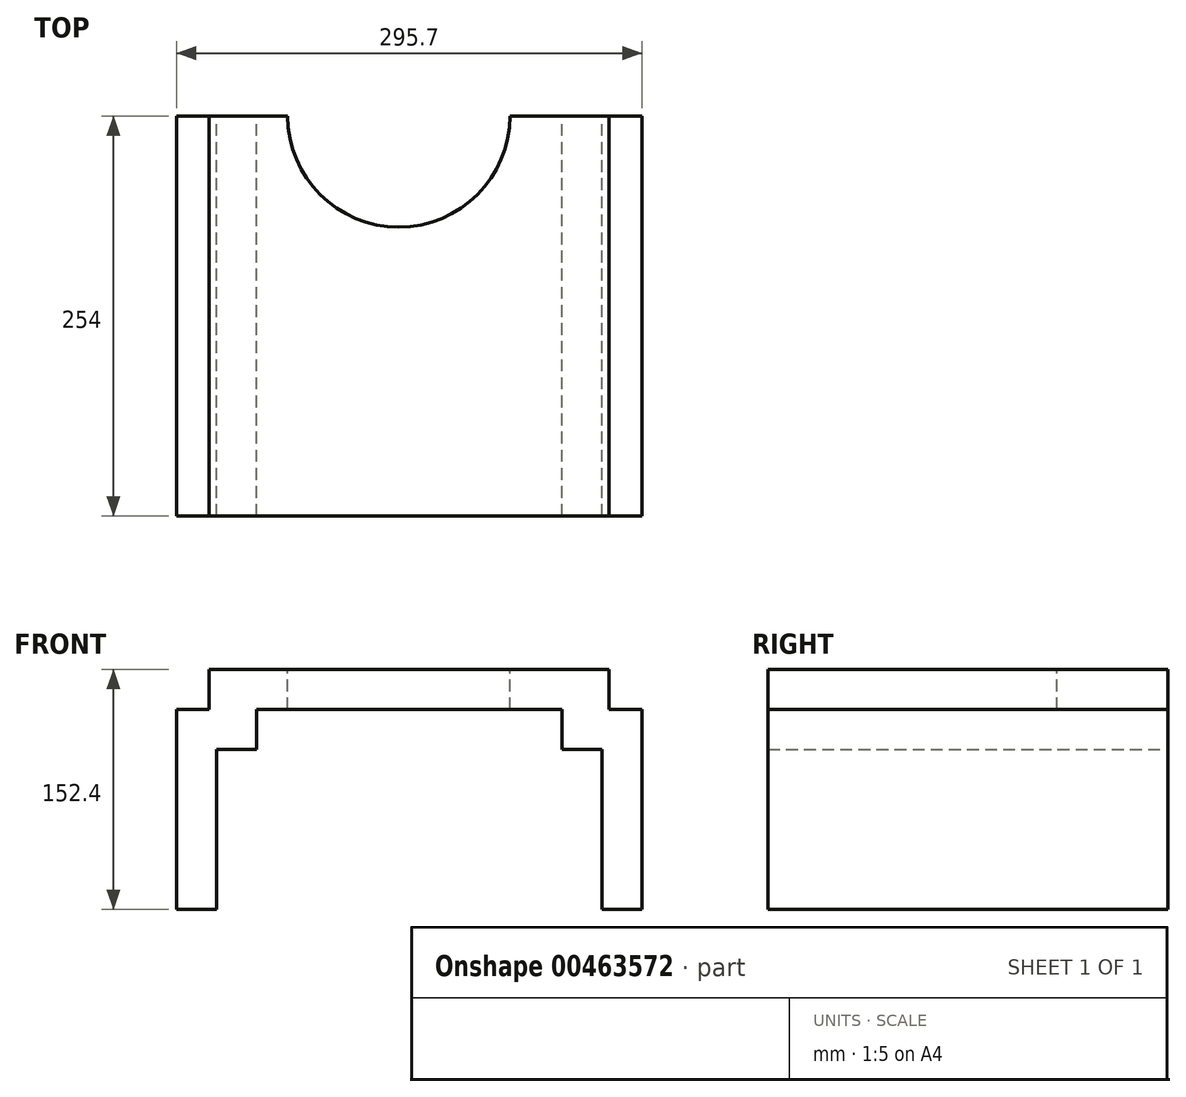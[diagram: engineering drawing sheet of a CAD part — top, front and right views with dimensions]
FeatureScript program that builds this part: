
annotation { "Feature Type Name" : "Feature", "Feature Type Description" : "" }
export const myFeature = defineFeature(function(context is Context, id is Id, definition is map)
    precondition{}
    {
        {
            var Q0;
            Q0=qCreatedBy(makeId("Front.planeOp"),FACE);
            var sketch = newSketch(context, id + "F0", { "sketchPlane" : qUnion([Q0])});
            skLineSegment(sketch, "E0.bottom", {"start": v(0, 0) * mm, "end": v(254, 0) * mm});
            skLineSegment(sketch, "E0.top", {"start": v(29.95, -25.4) * mm, "end": v(224.05, -25.4) * mm});
            skLineSegment(sketch, "E0.left", {"start": v(0, 0) * mm, "end": v(0, -25.4) * mm});
            skLineSegment(sketch, "E0.right", {"start": v(254, 0) * mm, "end": v(254, -25.4) * mm});
            skLineSegment(sketch, "E1.bottom", {"start": v(0, -25.4) * mm, "end": v(-20.85, -25.4) * mm});
            skLineSegment(sketch, "E1.top", {"start": v(4.55, -152.4) * mm, "end": v(-20.85, -152.4) * mm});
            skLineSegment(sketch, "E1.left", {"start": v(29.95, -25.4) * mm, "end": v(29.95, -50.8) * mm});
            skLineSegment(sketch, "E1.right", {"start": v(-20.85, -25.4) * mm, "end": v(-20.85, -152.4) * mm});
            skLineSegment(sketch, "E2", {"start": v(127, 79) * mm, "end": v(127, -89.42) * mm, "construction": true});
            skLineSegment(sketch, "E3", {"start": v(29.95, -50.8) * mm, "end": v(4.55, -50.8) * mm});
            skLineSegment(sketch, "E4", {"start": v(4.55, -50.8) * mm, "end": v(4.55, -152.4) * mm});
            skPoint(sketch, "E5.orphan", {"position": v(29.95, -152.4) * mm});
            skLineSegment(sketch, "E6.MirrorCS", {"start": v(254, -25.4) * mm, "end": v(274.85, -25.4) * mm});
            skLineSegment(sketch, "E7.MirrorCS", {"start": v(274.85, -25.4) * mm, "end": v(274.85, -152.4) * mm});
            skLineSegment(sketch, "E8.MirrorCS", {"start": v(249.45, -152.4) * mm, "end": v(274.85, -152.4) * mm});
            skLineSegment(sketch, "E9.MirrorCS", {"start": v(249.45, -50.8) * mm, "end": v(249.45, -152.4) * mm});
            skLineSegment(sketch, "E10.MirrorCS", {"start": v(224.05, -50.8) * mm, "end": v(249.45, -50.8) * mm});
            skLineSegment(sketch, "E11.MirrorCS", {"start": v(224.05, -25.4) * mm, "end": v(224.05, -50.8) * mm});
            skSolve(sketch);
        }
        {
            var Q0;
            Q0 = qSketchRegion(id + "F0", true);
            extrude(context, id + "F1", {"entities" : qUnion([Q0]), "depth" : 254 * mm});
        }
        {
            var Q0;
            Q0=makeQuery(id+"F1.opExtrude","SWEPT_FACE",FACE,{"disambiguationData":[OSD([sQuery(id+"F0.wireOp",EDGE,"E0.bottom")])]});
            var sketch = newSketch(context, id + "F2", { "sketchPlane" : qUnion([Q0])});
            skArc(sketch, "E12", {"start": v(49.85, 0) * mm, "mid": v(120.42, -70.57) * mm, "end": v(191, 0) * mm});
            skLineSegment(sketch, "E13", {"start": v(191, 0) * mm, "end": v(49.85, 0) * mm});
            skSolve(sketch);
        }
        {
            var Q0;
            Q0 = qSketchRegion(id + "F2", true);
            extrude(context, id + "F3", {"entities" : qUnion([Q0]), "operationType" : NewBodyOperationType.REMOVE, "endBound" : BoundingType.THROUGH_ALL, "oppositeDirection" : true, "depth" : 25.4 * mm});
        }
    });
